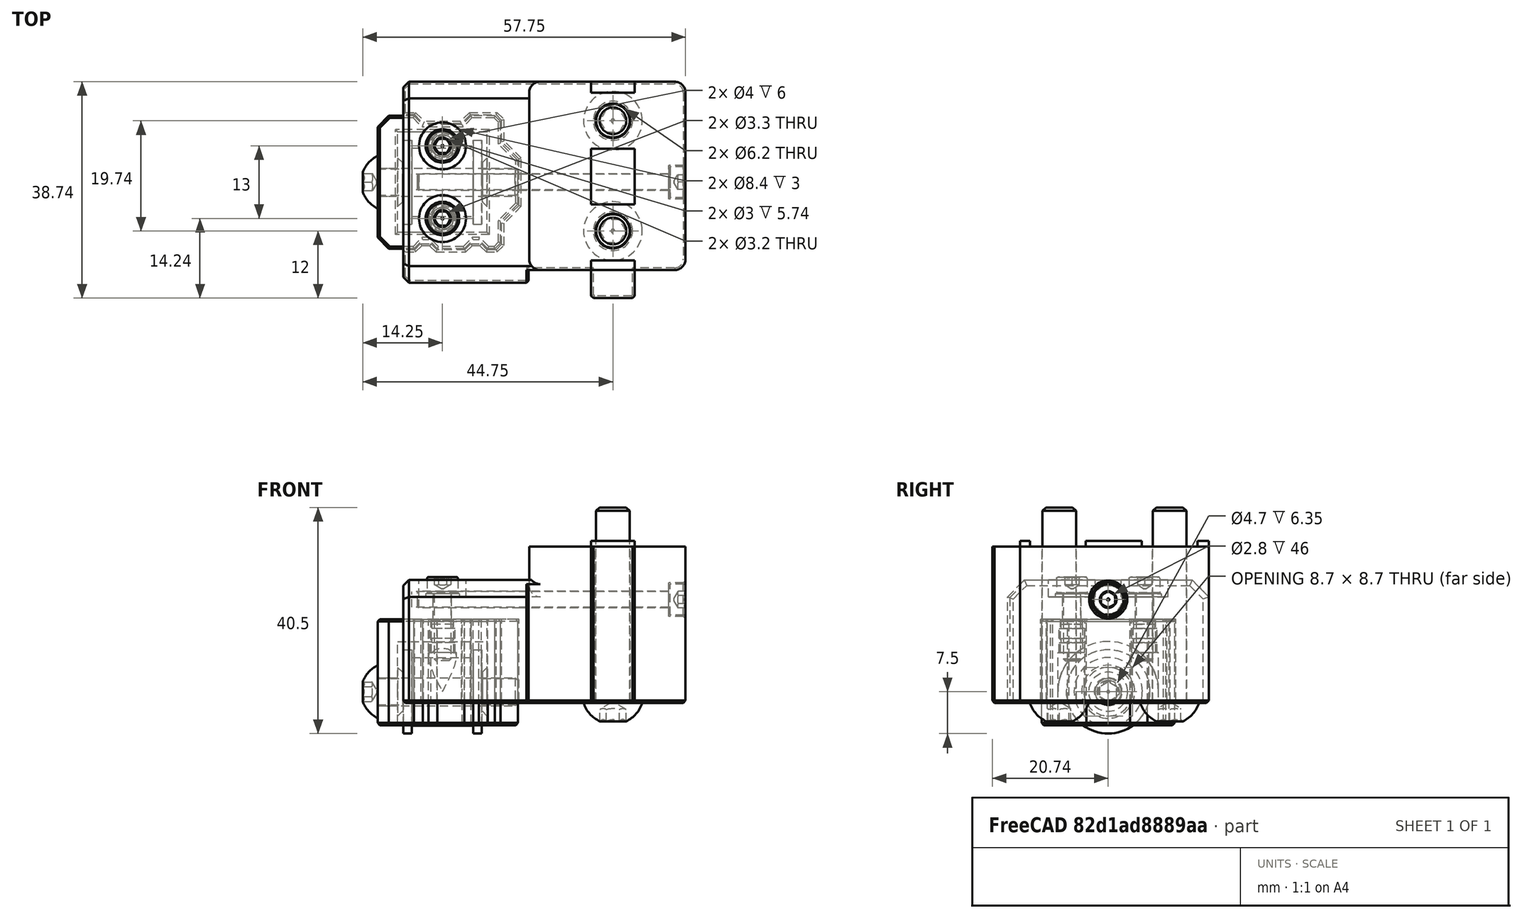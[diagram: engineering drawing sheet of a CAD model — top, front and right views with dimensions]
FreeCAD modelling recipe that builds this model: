
FCSTD DOCUMENT  (FreeCAD 0.19R24291 (Git))
Label: z-idler-right-assembly
License: Other
LicenseURL: GPL3
objects: Part::FeaturePython×10, Part::Feature×3, PartDesign::CoordinateSystem×1, App::Part×1
note: 14 computed .brp shape members not serialized (recipe doc carries the construction recipe); baked Part::Feature solids carry a one-line shape summary decoded from their .brp

FEATURE [Part::Feature] Part__Mirroring002002  label="20t-9mm-idler"
  Placement = pos=(0,0,-1) rot=(0,0,1;0rad)
  shape: bbox 14 x 15 x 15 mm, 7 faces (baked)
FEATURE [Part::FeaturePython] Washer002  label="M3-Washer007"  # Fasteners workbench fastener (typed FeaturePython)
  Placement = pos=(-15.5,6.5,19) rot=(0,0,1;0rad)
  diameter = 4
  invert = true
  matchOuter = true
  offset = 0
  type = 5
FEATURE [Part::FeaturePython] Washer003  label="M3-Washer008"  # Fasteners workbench fastener (typed FeaturePython)
  Placement = pos=(-15.5,-6.5,19) rot=(0,0,1;0rad)
  diameter = 4
  invert = true
  matchOuter = true
  offset = 0
  type = 5
FEATURE [Part::FeaturePython] Screw005  label="M3x45-Screw001"  # Fasteners workbench fastener (typed FeaturePython)
  Placement = pos=(25,0,18.5) rot=(0,1,0;1.5708rad)
  diameter = 4
  invert = false
  length = 10
  lengthCustom = 45
  matchOuter = true
  offset = 0
  thread = false
  type = 33
FEATURE [Part::FeaturePython] Screw006  label="M6x35-Screw003"  # Fasteners workbench fastener (typed FeaturePython)
  Placement = pos=(15,-8.74,0) rot=(1,0,0;3.14159rad)
  diameter = 4
  invert = false
  length = 13
  lengthCustom = 35
  matchOuter = true
  offset = 0
  thread = false
  type = 39
FEATURE [Part::FeaturePython] Screw007  label="M6x35-Screw002"  # Fasteners workbench fastener (typed FeaturePython)
  Placement = pos=(15,11,0) rot=(1,0,0;3.14159rad)
  diameter = 4
  invert = false
  length = 13
  lengthCustom = 35
  matchOuter = true
  offset = 0
  thread = false
  type = 39
FEATURE [Part::FeaturePython] Screw008  label="M3x12-Screw"  # Fasteners workbench fastener (typed FeaturePython)
  Placement = pos=(-15.5,6.5,19.55) rot=(0,0,1;0rad)
  baseObject = -> Washer002 [Edge1]
  diameter = 4
  invert = false
  length = 10
  lengthCustom = 12
  matchOuter = true
  offset = 0
  thread = false
  type = 33
FEATURE [Part::FeaturePython] Screw009  label="M3x12-Screw006"  # Fasteners workbench fastener (typed FeaturePython)
  Placement = pos=(-15.5,-6.5,19.55) rot=(0,0,1;0rad)
  baseObject = -> Washer003 [Edge1]
  diameter = 4
  invert = false
  length = 10
  lengthCustom = 12
  matchOuter = true
  offset = 0
  thread = false
  type = 33
FEATURE [Part::FeaturePython] Screw010  label="M5x25-Screw001"  # Fasteners workbench fastener (typed FeaturePython)
  Placement = pos=(-27,0,2) rot=(0,-1,0;1.5708rad)
  diameter = 3
  invert = false
  length = 6
  lengthCustom = 25
  matchOuter = true
  offset = 0
  thread = false
  type = 39
FEATURE [Part::Feature] Part__Mirroring002006001  label="z-idler-housing-right"
  shape: bbox 25.1 x 23.8 x 19 mm, 95 faces (baked)
FEATURE [Part::FeaturePython] HeatSet002  label="M3x4-HeatSet003"  # WARN: FeaturePython — macro-defined, semantics opaque (R4)
  Placement = pos=(-15.5,-6.5,9) rot=(1,0,0;3.14159rad)
  baseObject = -> Part__Mirroring002006001 [Edge76]
  diameter = 2
  invert = false
  offset = 6
FEATURE [Part::FeaturePython] HeatSet003  label="M3x4-HeatSet002"  # WARN: FeaturePython — macro-defined, semantics opaque (R4)
  Placement = pos=(-15.5,6.5,9) rot=(1,0,0;3.14159rad)
  baseObject = -> Part__Mirroring002006001 [Edge77]
  diameter = 2
  invert = false
  offset = 6
FEATURE [PartDesign::CoordinateSystem] LCS_Z_idler_right  label="LCS_Z-idler-right"
  AttacherType = Attacher::AttachEngine3D
FEATURE [Part::Feature] Part__Mirroring001  label="z-idler-mounter-right"
  shape: bbox 50.5 x 38.74 x 29 mm, 120 faces (baked)
FEATURE [App::Part] Part001  label="Z-idler-right"
  Group = -> [Part__Mirroring002002,Screw005,Screw007,Screw006,Screw008,Screw009,Washer003,Washer002,Screw010,Part__Mirroring002006001,HeatSet003,HeatSet002,LCS_Z_idler_right,Part__Mirroring001]
  Origin = -> Origin001
